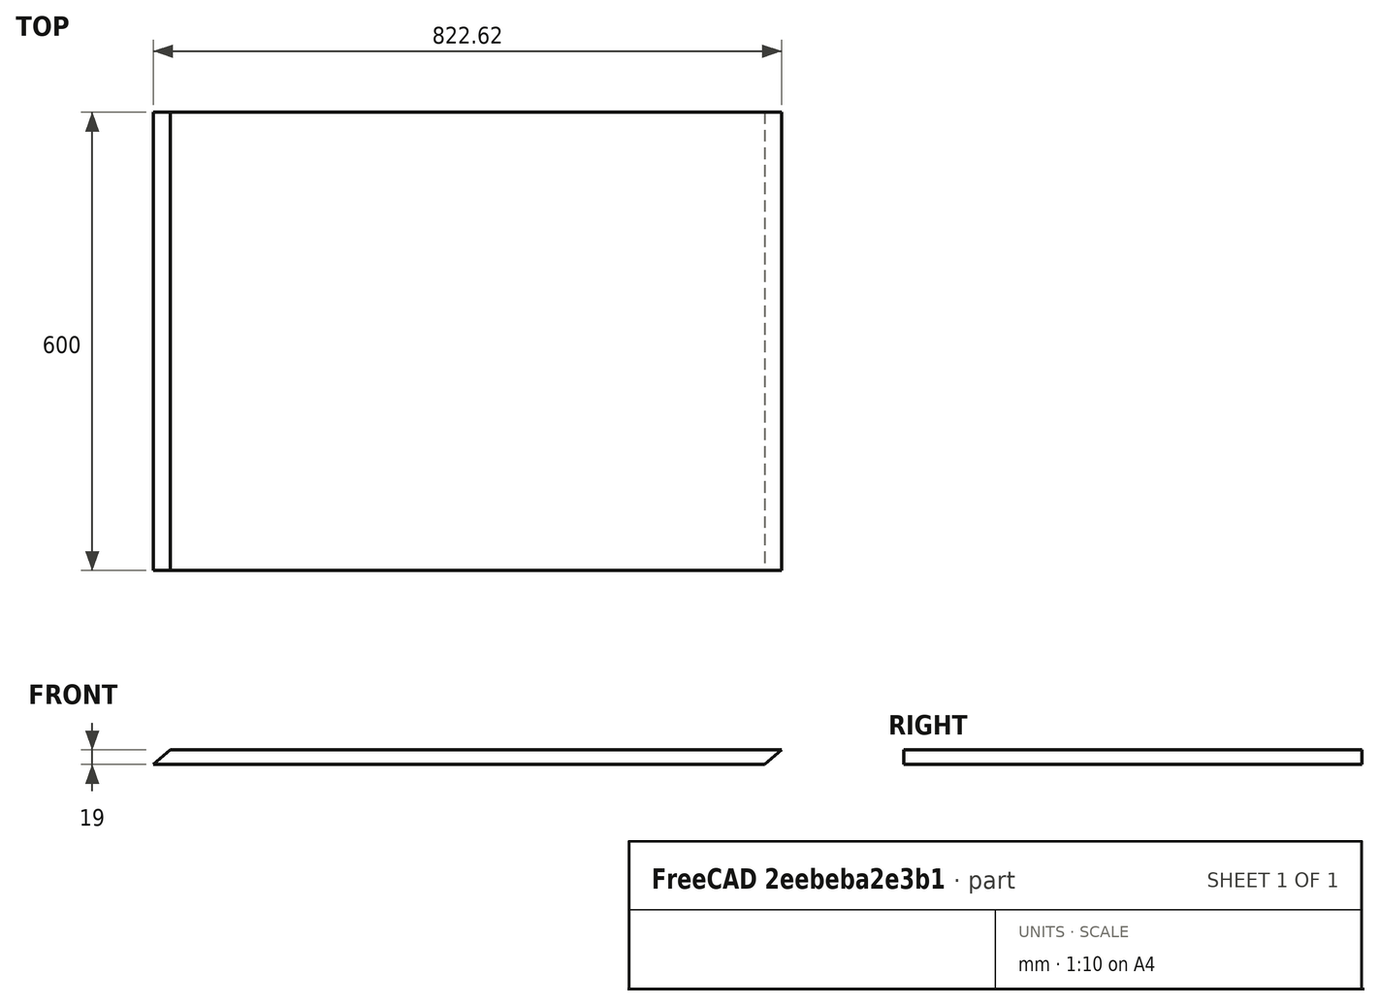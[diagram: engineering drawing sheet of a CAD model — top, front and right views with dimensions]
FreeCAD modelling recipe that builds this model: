
FCSTD DOCUMENT  (FreeCAD 1.0RUnknown)
Label: wardrobe_top_corpus03_jan
License: All rights reserved
objects: TechDraw::DrawViewDimension×5, PartDesign::CoordinateSystem×3, TechDraw::DrawProjGroupItem×2, Sketcher::SketchObject×1, PartDesign::Pad×1, PartDesign::Body×1, App::Part×1, TechDraw::DrawSVGTemplate×1, TechDraw::DrawPage×1
note: 18 computed .brp shape members not serialized (recipe doc carries the construction recipe); baked Part::Feature solids carry a one-line shape summary decoded from their .brp
EXTERNAL_REF file=../../mastersheet.FCStd obj=Spreadsheet
EXTERNAL_REF file=../../mastersketch.FCStd obj=Sketch

FEATURE [Sketcher::SketchObject] Sketch
  ArcFitTolerance = 1e-06
  AttachmentSupport = -> [XZ_Plane]
  FullyConstrained = true
  MakeInternals = false
  MapMode = 5
  Placement = pos=(0,0,0) rot=(1,0,0;1.5708rad)
  expr: Constraints[14] = mastersketch#Sketch.Constraints.alpha
  expr: Constraints[22] = (mastersketch#Sketch.Constraints.corpus03_door_width + 5 mm) / cos(mastersketch#Sketch.Constraints.alpha - 90 °)
  expr: Constraints[3] = mastersheet#Spreadsheet.corpus_outer_thickness
  sketch-geometry (9):
    g0: LineSegment StartX=-411.308 StartY=-9.5 StartZ=0 EndX=389.076 EndY=-9.5 EndZ=0
    g1: LineSegment StartX=411.308 StartY=9.5 StartZ=0 EndX=-389.076 EndY=9.5 EndZ=0
    g2: GeomPoint [constr] X=0 Y=0 Z=0
    g3: LineSegment StartX=-411.308 StartY=-9.5 StartZ=0 EndX=-389.076 EndY=9.5 EndZ=0
    g4: LineSegment StartX=411.308 StartY=9.5 StartZ=0 EndX=389.076 EndY=-9.5 EndZ=0
    g5: LineSegment [constr] StartX=0 StartY=0 StartZ=0 EndX=0 EndY=9.5 EndZ=0
    g6: LineSegment [constr] StartX=0 StartY=0 StartZ=0 EndX=0 EndY=-9.5 EndZ=0
    g7: LineSegment [constr] StartX=0 StartY=0 StartZ=0 EndX=-400.192 EndY=-3e-16 EndZ=0
    g8: LineSegment [constr] StartX=0 StartY=0 StartZ=0 EndX=400.192 EndY=7.9e-15 EndZ=0
  constraints (24):
    c: Horizontal(g0)
    c: Horizontal(g1)
    c: Coincident(g2,g-1)
    c: Distance(g0,g1) = 19
    c: Coincident(g1,g3)
    c: Coincident(g0,g4)
    c: Parallel(g3,g4)
    c: Coincident(g4,g1)
    c: Coincident(g5,g2)
    c: PointOnObject(g5,g1)
    c: Vertical(g5)
    c: Vertical(g6)
    c: Equal(g5,g6)
    c: Coincident(g0,g3)
    c: Angle(g3,g1) = 2.43442
    c: PointOnObject(g6,g0)
    c: Coincident(g6,g2)
    c: Coincident(g7,g2)
    c: Symmetric(g3,g3,g7)
    c: Coincident(g8,g2)
    c: Symmetric(g4,g4,g8)
    c: Equal(g7,g8)
    c: DistanceX(g0,g0) = 800.385
    c: DistanceX(g0,g1) = 822.617  'max_length'
FEATURE [PartDesign::Pad] Pad
  Direction = (0,-1,2e-16)
  Length = 600
  Length2 = 10
  Placement = pos=(0,0,0) rot=(1,0,0;1.5708rad)
  Profile = -> Sketch
  ReferenceAxis = -> Sketch [N_Axis]
  Refine = true
  Suppressed = false
  Type = 0
  expr: Length = mastersheet#Spreadsheet.corpus_depth
FEATURE [PartDesign::Body] Body  label="wardrobe_top_corpus03_jan"
  AllowCompound = false
  Group = -> [Sketch,Pad]
  Origin = -> Origin
  Tip = -> Pad
FEATURE [PartDesign::CoordinateSystem] LCS_1
  AttacherType = Attacher::AttachEngine3D
  AttachmentSupport = -> [Pad]
  MapMode = 45
  Placement = pos=(-411.308,-300,-9.5) rot=(0,0.707107,0.707107;3.14159rad)
FEATURE [PartDesign::CoordinateSystem] LCS_Origin
  AttacherType = Attacher::AttachEngine3D
  AttachmentSupport = -> [X_Axis001]
  MapMode = 2
FEATURE [PartDesign::CoordinateSystem] LCS_2
  AttacherType = Attacher::AttachEngine3D
  AttachmentSupport = -> [Pad]
  MapMode = 7
  Placement = pos=(-389.076,-600,9.5) rot=(0.57735,0.57735,0.57735;2.0944rad)
FEATURE [App::Part] wardrobe_top_corpus03_jan  label="wardrobe_top_corpus03_jan001"
  DrawingName = wardrobe_top_corpus03_jan.FCStd
  Group = -> [LCS_Origin,LCS_2,LCS_1,Body]
  Origin = -> Origin001
  PartDescription = wardrobe_top_corpus03_jan
  PartID = wardrobe_top_corpus03_jan
FEATURE [TechDraw::DrawSVGTemplate] Template  label="Vorlage"
  Height = 210
  Orientation = 1
  Template = <userpath>/scoop/apps/freecad/current/data/Mod/TechDraw/Templates/A4_Landscape_TD.svg
  Width = 297
FEATURE [TechDraw::DrawProjGroupItem] View
  CoarseView = false
  Direction = (0,-1,0)
  Focus = 100
  HardHidden = false
  IsoCount = 0
  IsoHidden = false
  IsoVisible = false
  LockPosition = false
  Perspective = false
  Rotation = 0
  RotationVector = (1,0,0)
  Scale = 0.1
  ScaleType = 2
  ScrubCount = 1
  SeamHidden = false
  SeamVisible = false
  SmoothHidden = false
  SmoothVisible = true
  Source = -> [wardrobe_top_corpus03_jan]
  Type = 0
  X = 179.23
  XDirection = (1e-16,0,-1)
  Y = 137.322
FEATURE [TechDraw::DrawProjGroupItem] View001
  CoarseView = false
  Direction = (0,0,-1)
  Focus = 100
  HardHidden = false
  IsoCount = 0
  IsoHidden = false
  IsoVisible = false
  LockPosition = false
  Perspective = false
  Rotation = 0
  RotationVector = (1,0,0)
  Scale = 0.1
  ScaleType = 2
  ScrubCount = 1
  SeamHidden = false
  SeamVisible = false
  SmoothHidden = false
  SmoothVisible = true
  Source = -> [wardrobe_top_corpus03_jan]
  Type = 0
  X = 80.4098
  XDirection = (-3e-16,1,0)
  Y = 137.322
FEATURE [TechDraw::DrawViewDimension] Dimension  label="Maß"
  AngleOverride = false
  Arbitrary = false
  ArbitraryTolerances = false
  BoxCorners = (2) [(-30,-41.1308,0),(30,41.1308,0)]
  EqualTolerance = true
  ExtensionAngle = 0
  FormatSpec = %.1w
  FormatSpecOverTolerance = %+.1w
  FormatSpecUnderTolerance = %+.1w
  Inverted = false
  LineAngle = 0
  LockPosition = false
  MeasureType = 1
  OverTolerance = 0
  References2D = -> [View001]
  Rotation = 0
  ScaleType = 0
  TheoreticalExact = false
  Type = 1
  UnderTolerance = 0
  X = 0
  Y = -46.7106
FEATURE [TechDraw::DrawViewDimension] Dimension001  label="Maß001"
  AngleOverride = false
  Arbitrary = false
  ArbitraryTolerances = false
  BoxCorners = (2) [(-30,-41.1308,0),(30,41.1308,0)]
  EqualTolerance = true
  ExtensionAngle = 0
  FormatSpec = %.1w
  FormatSpecOverTolerance = %+.1w
  FormatSpecUnderTolerance = %+.1w
  Inverted = false
  LineAngle = 0
  LockPosition = false
  MeasureType = 1
  OverTolerance = 0
  References2D = -> [View001]
  Rotation = 0
  ScaleType = 0
  TheoreticalExact = false
  Type = 0
  UnderTolerance = 0
  X = 51.2409
  Y = -10.3819
FEATURE [TechDraw::DrawViewDimension] Dimension003  label="Maß003"
  AngleOverride = false
  Arbitrary = false
  ArbitraryTolerances = false
  BoxCorners = (2) [(-0.95,-41.1308,0),(0.95,41.1308,0)]
  EqualTolerance = true
  ExtensionAngle = 0
  FormatSpec = %.1w
  FormatSpecOverTolerance = %+.1w
  FormatSpecUnderTolerance = %+.1w
  Inverted = false
  LineAngle = 0
  LockPosition = false
  MeasureType = 1
  OverTolerance = 0
  References2D = -> [View]
  Rotation = 0
  ScaleType = 0
  TheoreticalExact = false
  Type = 6
  UnderTolerance = 0
  X = 16.0781
  Y = 5.68594
FEATURE [TechDraw::DrawViewDimension] Dimension004  label="Maß004"
  AngleOverride = false
  Arbitrary = false
  ArbitraryTolerances = false
  BoxCorners = (2) [(-0.95,-41.1308,0),(0.95,41.1308,0)]
  EqualTolerance = true
  ExtensionAngle = 0
  FormatSpec = %.1w
  FormatSpecOverTolerance = %+.1w
  FormatSpecUnderTolerance = %+.1w
  Inverted = false
  LineAngle = 0
  LockPosition = false
  MeasureType = 1
  OverTolerance = 0
  References2D = -> [View]
  Rotation = 0
  ScaleType = 0
  TheoreticalExact = false
  Type = 0
  UnderTolerance = 0
  X = 9.01033
  Y = 59.2546
FEATURE [TechDraw::DrawViewDimension] Dimension006  label="Maß006"
  AngleOverride = false
  Arbitrary = false
  ArbitraryTolerances = false
  BoxCorners = (2) [(-0.95,-41.1308,0),(0.95,41.1308,0)]
  EqualTolerance = true
  ExtensionAngle = 0
  FormatSpec = %.1w
  FormatSpecOverTolerance = %+.1w
  FormatSpecUnderTolerance = %+.1w
  Inverted = false
  LineAngle = 0
  LockPosition = false
  MeasureType = 1
  OverTolerance = 0
  References2D = -> [View]
  Rotation = 0
  ScaleType = 0
  TheoreticalExact = false
  Type = 6
  UnderTolerance = 0
  X = -16.1416
  Y = 14.6144
FEATURE [TechDraw::DrawPage] Page  label="Seite"
  KeepUpdated = true
  NextBalloonIndex = 1
  ProjectionType = 0
  Template = -> Template
  Views = -> [View,View001,Dimension,Dimension001,Dimension003,Dimension004,Dimension006]
